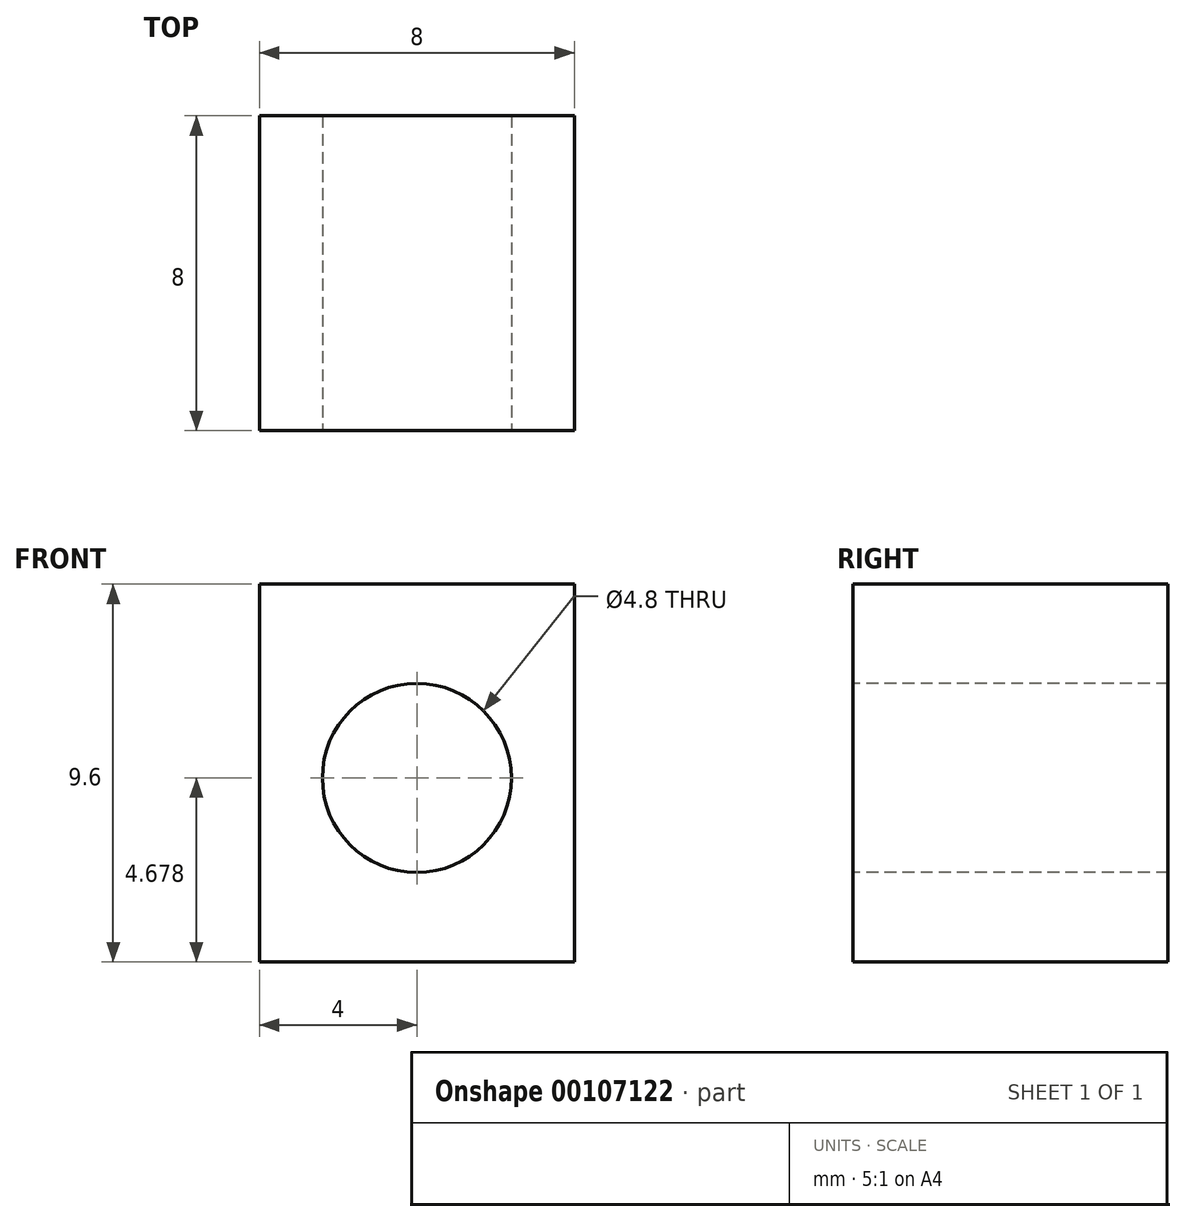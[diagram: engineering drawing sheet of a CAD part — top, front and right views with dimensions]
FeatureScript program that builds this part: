
annotation { "Feature Type Name" : "Feature", "Feature Type Description" : "" }
export const myFeature = defineFeature(function(context is Context, id is Id, definition is map)
    precondition{}
    {
        {
            var Q0;
            Q0=qCreatedBy(makeId("Top.planeOp"),FACE);
            var sketch = newSketch(context, id + "F0", { "sketchPlane" : qUnion([Q0])});
            skCircle(sketch, "E0.cCircle", {"center": v(0, 0) * mm, "radius": 4 * mm, "construction": true});
            skLineSegment(sketch, "E0.0", {"start": v(4, 4) * mm, "end": v(4, -4) * mm});
            skLineSegment(sketch, "E0.1", {"start": v(4, -4) * mm, "end": v(-4, -4) * mm});
            skLineSegment(sketch, "E0.2", {"start": v(-4, -4) * mm, "end": v(-4, 4) * mm});
            skLineSegment(sketch, "E0.3", {"start": v(-4, 4) * mm, "end": v(4, 4) * mm});
            skPoint(sketch, "E0.0.midPoint", {"position": v(4, 0) * mm});
            skSolve(sketch);
        }
        {
            var Q0;
            Q0=makeQuery(id+"F0.imprint","IMPRINT",FACE,{"disambiguationData":[TD([[makeQuery(id+"F0.imprint","IMPRINT",EDGE,{"derivedFrom":sQuery(id+"F0.wireOp",EDGE,"E0.0")}),-1.0]])]});
            extrude(context, id + "F1", {"entities" : qUnion([Q0]), "depth" : 9.6 * mm});
        }
        {
            var Q0;
            Q0=makeQuery(id+"F1.opExtrude","SWEPT_FACE",FACE,{"disambiguationData":[OSD([sQuery(id+"F0.wireOp",EDGE,"E0.1")])]});
            var sketch = newSketch(context, id + "F2", { "sketchPlane" : qUnion([Q0])});
            skLineSegment(sketch, "E1", {"start": v(0, 0) * mm, "end": v(0, 4.68) * mm, "construction": true});
            skCircle(sketch, "E2", {"center": v(0, 4.68) * mm, "radius": 2.4 * mm});
            skSolve(sketch);
        }
        {
            var Q0;
            Q0 = qSketchRegion(id + "F2", true);
            var Q1;
            Q1=sQuery(id+"F2.wireOp",EDGE,"E2");
            extrude(context, id + "F3", {"entities" : qUnion([Q0]), "operationType" : NewBodyOperationType.REMOVE, "surfaceEntities" : qUnion([Q1]), "oppositeDirection" : true, "depth" : 25 * mm});
        }
        {
            var Q0;
            Q0=makeQuery(id+"F1.opExtrude","CAP_FACE",FACE,{"disambiguationData":[OSD([sQuery(id+"F0.wireOp",EDGE,"E0.0"),sQuery(id+"F0.wireOp",EDGE,"E0.1"),sQuery(id+"F0.wireOp",EDGE,"E0.2"),sQuery(id+"F0.wireOp",EDGE,"E0.3")])],"isStart":false});
            var sketch = newSketch(context, id + "F4", { "sketchPlane" : qUnion([Q0])});
            skLineSegment(sketch, "E3", {"start": v(0, -4) * mm, "end": v(0, 0) * mm});
            skCircle(sketch, "E4", {"center": v(0, 0) * mm, "radius": 2.4 * mm});
            skSolve(sketch);
        }
        {
            var Q0;
            Q0=sQuery(id+"F4.wireOp",EDGE,"E4");
            extrude(context, id + "F5", {"bodyType" : ToolBodyType.SURFACE, "surfaceEntities" : qUnion([Q0]), "depth" : 1.6 * mm});
        }
    });
